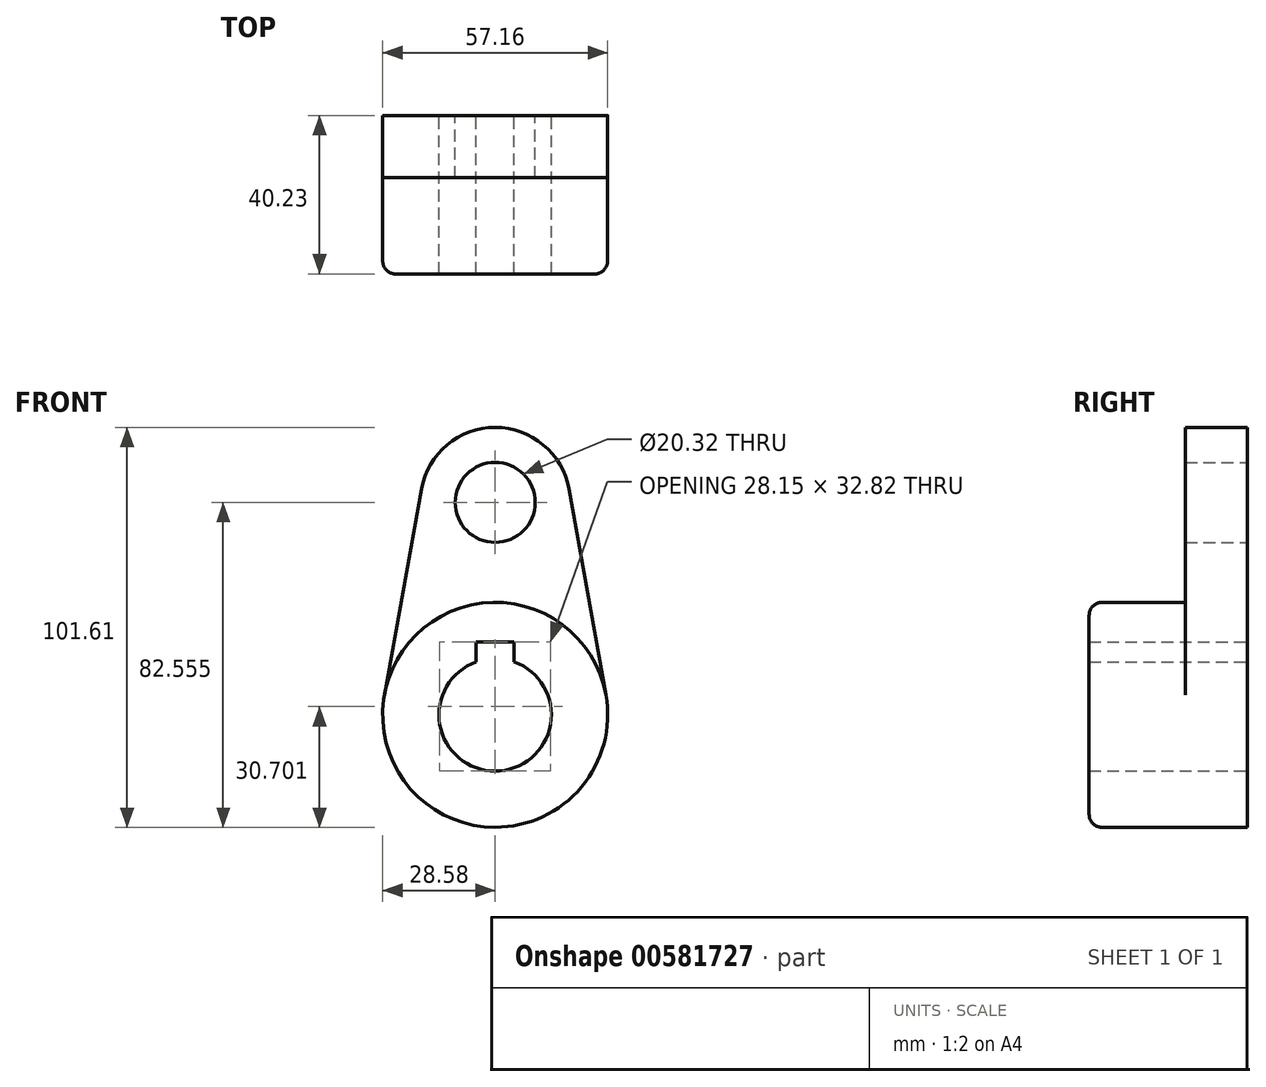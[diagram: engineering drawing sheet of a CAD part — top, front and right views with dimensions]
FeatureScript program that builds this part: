
annotation { "Feature Type Name" : "Feature", "Feature Type Description" : "" }
export const myFeature = defineFeature(function(context is Context, id is Id, definition is map)
    precondition{}
    {
        {
            var Q0;
            Q0=qCreatedBy(makeId("Front.planeOp"),FACE);
            var sketch = newSketch(context, id + "F0", { "sketchPlane" : qUnion([Q0])});
            skArc(sketch, "E0", {"start": v(-4.83, 13.45) * mm, "mid": v(0, -14.29) * mm, "end": v(4.83, 13.45) * mm});
            skCircle(sketch, "E1", {"center": v(0, 53.98) * mm, "radius": 10.16 * mm});
            skLineSegment(sketch, "E2", {"start": v(-4.83, 13.45) * mm, "end": v(-4.83, 18.53) * mm});
            skLineSegment(sketch, "E3", {"start": v(-4.83, 18.53) * mm, "end": v(4.83, 18.53) * mm});
            skLineSegment(sketch, "E4", {"start": v(4.83, 18.53) * mm, "end": v(4.83, 13.45) * mm});
            skCircle(sketch, "E5", {"center": v(0, 0) * mm, "radius": 28.58 * mm});
            skArc(sketch, "E6", {"start": v(18.75, 57.34) * mm, "mid": v(0, 73.03) * mm, "end": v(-18.75, 57.34) * mm});
            skLineSegment(sketch, "E7", {"start": v(-18.75, 57.34) * mm, "end": v(-28.13, 5.04) * mm});
            skLineSegment(sketch, "E8", {"start": v(18.75, 57.34) * mm, "end": v(28.13, 5.04) * mm});
            skSolve(sketch);
        }
        {
            var Q0;
            Q0=makeQuery(id+"F0.imprint","IMPRINT",FACE,{"disambiguationData":[TD([[makeQuery(id+"F0.imprint","IMPRINT",EDGE,{"derivedFrom":sQuery(id+"F0.wireOp",EDGE,"E0")}),-1.0]])]});
            extrude(context, id + "F1", {"entities" : qUnion([Q0]), "depth" : 40.23 * mm, "offsetDistance" : 25.4 * mm});
        }
        {
            var Q0;
            Q0 = qSketchRegion(id + "F0", true);
            extrude(context, id + "F2", {"entities" : qUnion([Q0]), "operationType" : NewBodyOperationType.ADD, "depth" : 15.77 * mm, "offsetDistance" : 25.4 * mm});
        }
        {
            var Q0;
            Q0=makeQuery(id+"F1.opExtrude","CAP_EDGE",EDGE,{"disambiguationData":[OSD([sQuery(id+"F0.wireOp",EDGE,"E5")])],"isStart":false});
            fillet(context, id + "F3", {"entities" : qUnion([Q0]), "radius" : 3.3 * mm, "tangentPropagation" : true, "allowEdgeOverflow" : false});
        }
    });
